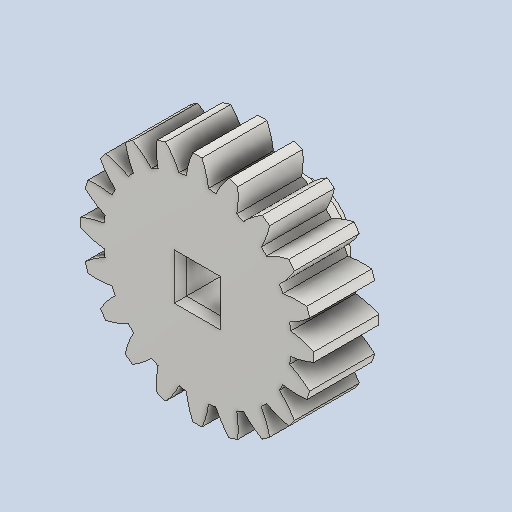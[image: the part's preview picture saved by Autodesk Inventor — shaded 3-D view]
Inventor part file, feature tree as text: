
AUTODESK INVENTOR PART (.ipt)
format: ipt  version: 2022 (Build 260153000, 153)  size: 577,536 bytes
history: native  units: mm (DEFAULTED — no unit token found)
features: sketch x4, extrude x3, plane x3, other x3, chamfer x2
ambient origin geometry x8: Origin, YZ Plane, XZ Plane, XY Plane, X Axis, Y Axis, Z Axis, Center Point
bodies: Solid1 (feature_tree)
feature tree (15):
  extrude  "Extrusion1"  Depth=6.35mm TaperAngle=0.0deg
  plane  "Work Plane1"
  plane  "Work Plane2"
  plane  "Work Plane3"
  other  "Spur Gear"
  extrude  "Extrusion2"  Depth=76.2mm TaperAngle=0.0deg
  extrude  "Extrusion3"  TaperAngle=0.0deg  [1 undecoded]
  chamfer  "Chamfer1"  Distance=25.4mm
  chamfer  "Chamfer2"  [1 undecoded]
  sketch  "Sketch1"  dims[d0=22.8mm d1=6.35mm d2=0.0mm]
  sketch  "Sketch2"  dims[d3=20.0mm d4=76.2mm d5=0.0mm]
  other  "Srf1"
  sketch  "Sketch3"  dims[d6=0.0mm d7=1.570796mm d9=0.0mm]
  sketch  "Sketch4"  dims[d14=0.0mm d15=25.4mm d16=0.0mm d17=0.0mm d18=0.0mm d19=25.4mm d20=3.325mm d21=0.0mm d22=0.0mm d23=9.525mm d24=5.112mm d25=0.0mm d26=1.2mm d27=3.175mm d28=45.0deg d29=0.6mm d30=3.175mm d31=45.0deg]
  other  "Pitch Diameter"
note: 2 required parameter values undecoded (feature->parameter linkage not recoverable at this tier; creation-order binding heuristic only, values carry confidence <= 0.55)
